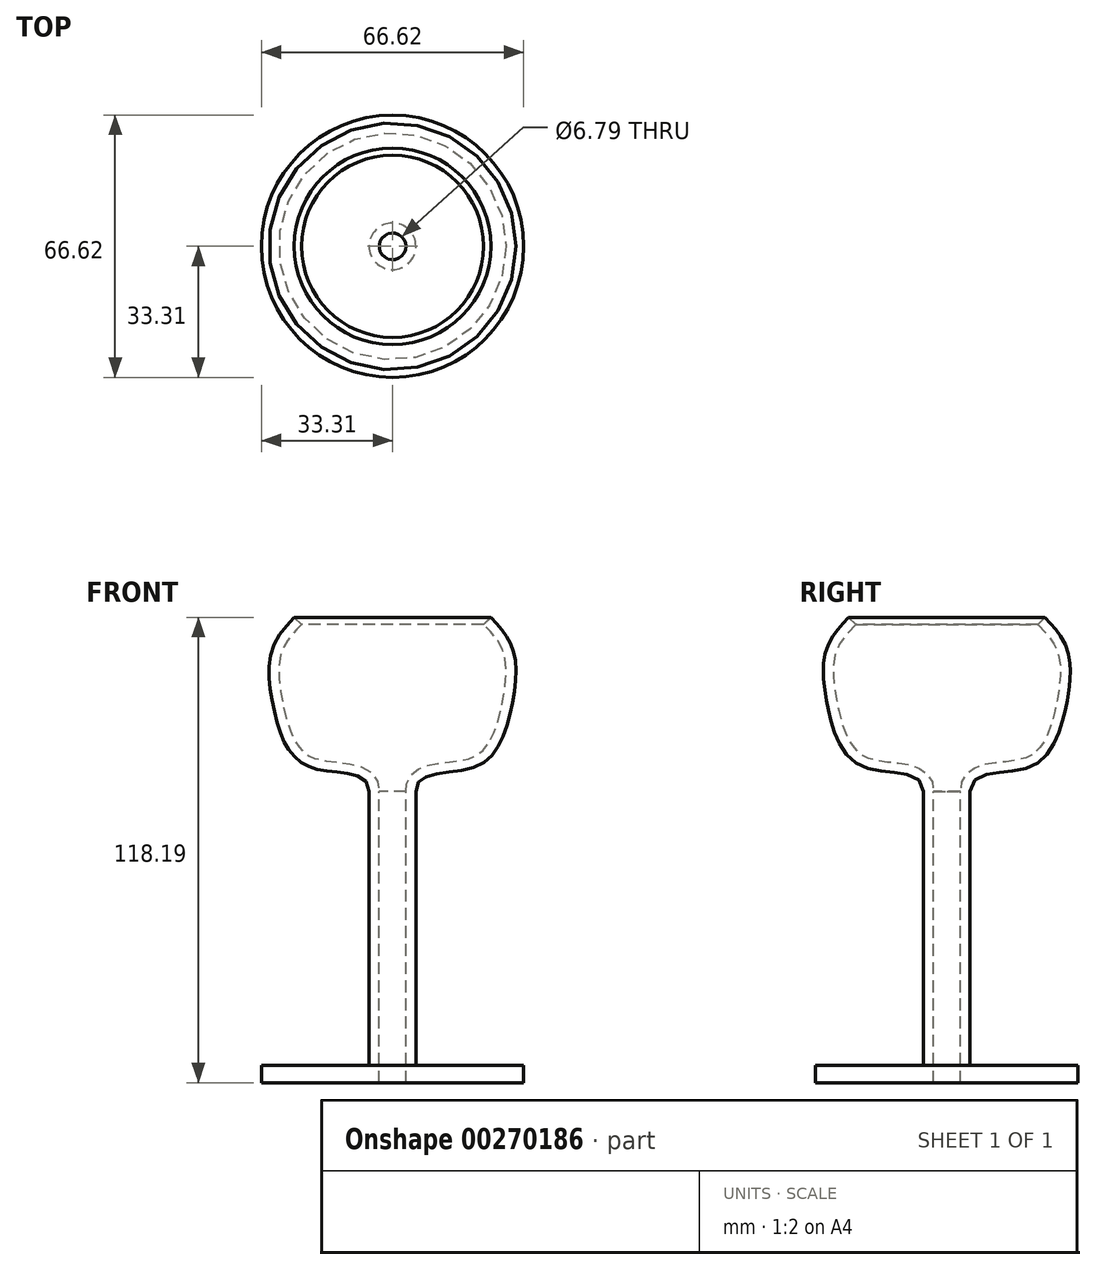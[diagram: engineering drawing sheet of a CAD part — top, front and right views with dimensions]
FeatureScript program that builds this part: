
annotation { "Feature Type Name" : "Feature", "Feature Type Description" : "" }
export const myFeature = defineFeature(function(context is Context, id is Id, definition is map)
    precondition{}
    {
        {
            var Q0;
            Q0=qCreatedBy(makeId("Front.planeOp"),FACE);
            var sketch = newSketch(context, id + "F0", { "sketchPlane" : qUnion([Q0])});
            skLineSegment(sketch, "E0", {"start": v(0, 70.48) * mm, "end": v(0, -56.52) * mm});
            skLineSegment(sketch, "E1", {"start": v(-3.4, -56.52) * mm, "end": v(-33.31, -56.52) * mm});
            skLineSegment(sketch, "E2", {"start": v(-33.31, -56.52) * mm, "end": v(-33.31, -52.07) * mm});
            skLineSegment(sketch, "E3", {"start": v(-33.31, -52.07) * mm, "end": v(-5.94, -52.07) * mm});
            skLineSegment(sketch, "E4", {"start": v(-5.94, -52.07) * mm, "end": v(-5.94, 17.48) * mm});
            skFitSpline(sketch, "E5", {"points": [v(-5.94, 17.48) * mm, v(-20.74, 23.57) * mm, v(-30.06, 37.96) * mm, v(-30.62, 53.48) * mm, v(-24.98, 61.67) * mm], "startDerivative": vector(0, 67.36) * mm, "endDerivative": vector(33.2, 35.08) * mm});
            skFitSpline(sketch, "E6.0", {"points": [v(-3.4, 17.48) * mm, v(-3.4, 17.99) * mm, v(-3.49, 18.99) * mm, v(-3.96, 20.4) * mm, v(-4.74, 21.62) * mm, v(-5.73, 22.57) * mm, v(-6.82, 23.27) * mm, v(-7.96, 23.77) * mm, v(-9.12, 24.13) * mm, v(-10.69, 24.48) * mm, v(-12.68, 24.77) * mm, v(-15.06, 25.02) * mm, v(-16.94, 25.26) * mm, v(-18.3, 25.5) * mm, v(-19.08, 25.7) * mm, v(-19.65, 25.87) * mm, v(-20.17, 26.06) * mm, v(-21.02, 26.43) * mm, v(-22.1, 27.1) * mm, v(-23.22, 28.13) * mm, v(-24.22, 29.38) * mm, v(-25.1, 30.86) * mm, v(-25.85, 32.53) * mm, v(-26.5, 34.36) * mm, v(-27.06, 36.3) * mm, v(-27.46, 37.97) * mm, v(-27.76, 39.32) * mm, v(-28.03, 40.66) * mm, v(-28.33, 42.3) * mm, v(-28.6, 44.21) * mm, v(-28.77, 46.05) * mm, v(-28.84, 47.8) * mm, v(-28.8, 49.42) * mm, v(-28.64, 50.92) * mm, v(-28.36, 52.27) * mm, v(-27.96, 53.46) * mm, v(-27.42, 54.58) * mm, v(-26.55, 56.03) * mm, v(-25.16, 57.78) * mm, v(-23.82, 59.19) * mm, v(-23.13, 59.92) * mm]});
            skLineSegment(sketch, "E6.1", {"start": v(-3.4, -52.07) * mm, "end": v(-3.4, 17.48) * mm});
            skLineSegment(sketch, "E7", {"start": v(-23.13, 59.92) * mm, "end": v(-24.98, 61.67) * mm});
            skLineSegment(sketch, "E8", {"start": v(-3.4, -52.07) * mm, "end": v(-3.4, -56.52) * mm});
            skSolve(sketch);
        }
        {
            var Q0;
            Q0 = qSketchRegion(id + "F0", true);
            var Q1;
            Q1=sQuery(id+"F0.wireOp",EDGE,"E0");
            revolve(context, id + "F1", {"entities" : qUnion([Q0]), "axis" : qUnion([Q1]), "revolveType" : RevolveType.FULL});
        }
    });
